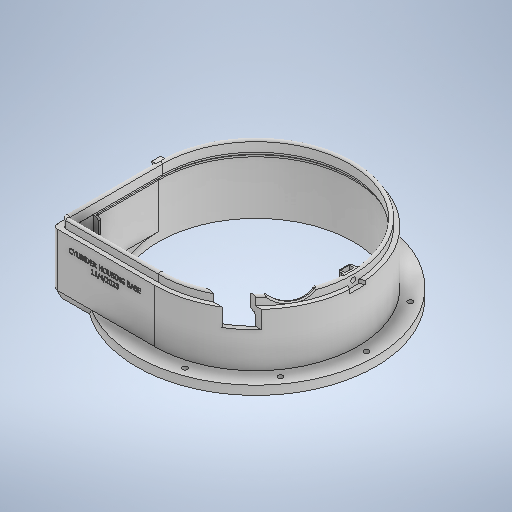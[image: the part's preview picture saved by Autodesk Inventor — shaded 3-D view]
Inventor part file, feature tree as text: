
AUTODESK INVENTOR PART (.ipt)
format: ipt  version: 2025 (Build 290162000, 162)  size: 1,285,632 bytes
history: native  units: mm
features: sketch x18, extrude x13, fillet x7, chamfer x5, hole x2, pattern_circular x1, other x1, plane x1, emboss x1
ambient origin geometry x8: Origin, YZ Plane, XZ Plane, XY Plane, X Axis, Y Axis, Z Axis, Center Point
bodies: Solid1 (feature_tree)
feature tree (49):
  extrude  "Base"  Depth=220.0mm
  hole  "Cylinder Mount Holes"  [1 undecoded]
  pattern_circular  "Circular Pattern1"  Count=10 Angle=360.0deg
  extrude  "Walls"  Depth=220.0mm
  extrude  "Corner Fill"  Depth=30.0mm TaperAngle=0.0deg
  fillet  "Corner Fillet"  Radius=5.0mm
  other  "Seal Groove"
  extrude  "Overhang for Lip"  Depth=3.0mm
  extrude  "Lip"  Depth=4.0mm
  chamfer  "Overhang Chamfer"  Distance=4.0mm
  fillet  "Overhang Fillet"  Radius=10.0mm
  extrude  "Nut Seat Body"  Depth=4.0mm
  chamfer  "Nut Seat Body Chamfer"  Distance=20.0mm
  extrude  "Nut Seat"  Depth=10.0mm
  extrude  "Front Alignment Tab"  Depth=1.0mm
  hole  "Bolt Holt"  [1 undecoded]
  extrude  "Hinge Tab"  Depth=4.0mm TaperAngle=0.0deg
  fillet  "Nut Seat Body Fillets"  Radius=7.5mm
  fillet  "Top Edge Fillet"  Radius=10.0mm
  sketch  "Sketch15"  dims[d49=12.7mm d50=0.0mm d59=6.0mm]
  extrude  "LV Window"  Depth=3.0mm
  fillet  "LV Window Fillet"  Radius=10.0mm
  plane  "Work Plane1"
  extrude  "8020 Ledge"  Depth=42.0mm
  extrude  "Ledge Walls"  Depth=22.0mm
  chamfer  "Ledge Chamfer"  [1 undecoded]
  fillet  "Ledge Fillets"  Radius=1.5mm
  chamfer  "Ledge Wall Chamfer"  [1 undecoded]
  extrude  "8020 Window"  Depth=10.0mm
  chamfer  "Bottom Corner Chamfer"  Distance=25.0mm
  fillet  "Hinge Tab Fillet"  Radius=88.16mm
  emboss  "Emboss1"
  sketch  "Sketch1"  dims[d0=270.0mm d1=220.0mm]
  sketch  "Sketch2"  dims[d2=10.0mm d3=0.0mm]
  sketch  "Sketch3"  dims[d4=5.5mm d5=6.0mm d6=4.0mm d7=2.0mm d8=90.0deg d9=8.0mm d10=20.594885mm d11=125.0mm d12=100.0mm d13=360.0deg]
  sketch  "Sketch4"  dims[d15=230.0mm d16=220.0mm]
  sketch  "Sketch6"  dims[d17=60.0mm d18=0.0mm d19=30.0mm d20=0.0mm d21=5.0mm]
  sketch  "Sketch7"  dims[d26=2.0mm d27=3.0mm]
  sketch  "Sketch8"  dims[d29=90.0deg d30=4.0mm d31=4.0mm d32=0.0mm d33=10.0mm d34=0.0mm]
  sketch  "Sketch9"  dims[d35=4.0mm d36=2.0mm d37=45.0deg d38=4.0mm]
  sketch  "Sketch10"  dims[d39=14.0mm]
  sketch  "Sketch12"  dims[d40=10.0mm d41=20.0mm d42=0.0mm]
  sketch  "Sketch13"  dims[d43=10.2mm d44=2.0mm d45=45.0deg d46=10.0mm]
  sketch  "Sketch14"  dims[d47=5.0mm d48=1.0mm]
  sketch  "Sketch16"  dims[d60=9.0mm d61=4.0mm d62=0.0mm]
  sketch  "Sketch18"  dims[d63=5.5mm d64=6.0mm d65=4.0mm d66=2.0mm d67=90.0deg d68=8.0mm d69=20.594885mm d70=7.5mm d71=10.0mm d72=0.0mm]
  sketch  "Sketch19"  dims[d73=1.0mm d74=3.0mm d75=10.0mm]
  sketch  "Sketch20"  dims[d76=2.0mm d77=42.0mm]
  sketch  "Sketch21"  dims[d78=53.266mm d79=22.0mm d80=0.0mm d81=0.0mm d82=1.5mm d85=-20.0mm d86=10.0mm d87=25.0mm d88=88.16mm d89=10.0mm d90=0.0mm d91=2.5mm d92=2.5mm d93=17.5mm d94=0.0mm d95=10.0mm d96=2.0mm d97=45.0deg d98=2.0mm d99=3.0mm d100=2.0mm d101=45.0deg d102=30.0mm d103=20.0mm d104=88.16mm d105=0.0mm d106=0.0mm d107=114.0mm d108=5.0mm d109=10.0mm d110=45.0deg d111=0.15mm d112=1.0mm d113=0.0mm]
note: 4 required parameter values undecoded (feature->parameter linkage not recoverable at this tier; creation-order binding heuristic only, values carry confidence <= 0.55)
